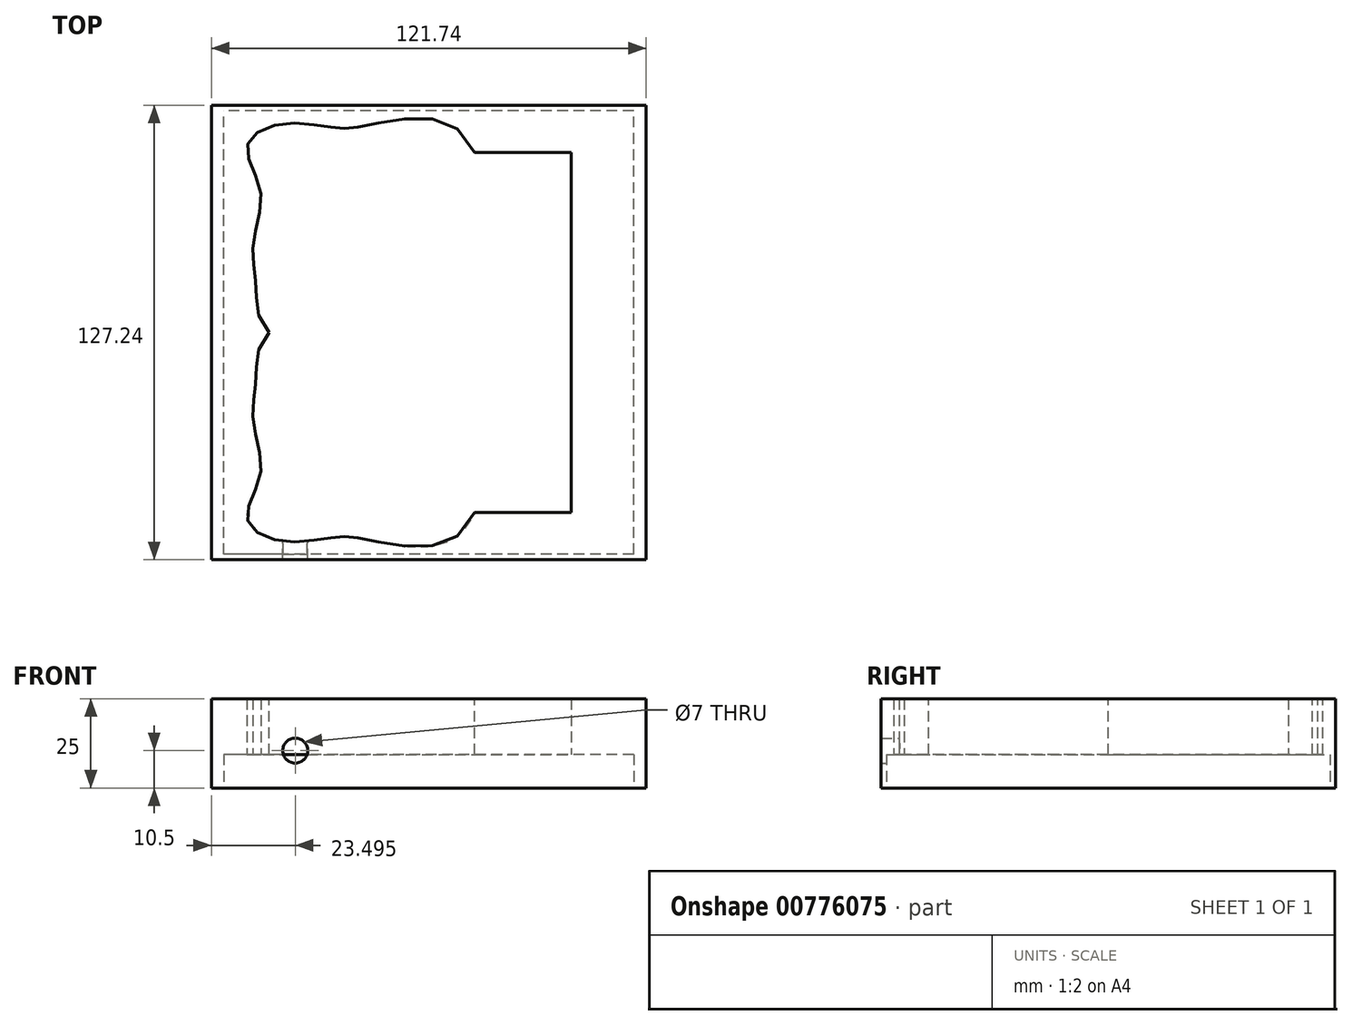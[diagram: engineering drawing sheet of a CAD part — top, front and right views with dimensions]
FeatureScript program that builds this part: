
annotation { "Feature Type Name" : "Feature", "Feature Type Description" : "" }
export const myFeature = defineFeature(function(context is Context, id is Id, definition is map)
    precondition{}
    {
        {
            var Q0;
            Q0=qCreatedBy(makeId("Top.planeOp"),FACE);
            var sketch = newSketch(context, id + "F0", { "sketchPlane" : qUnion([Q0])});
            skLineSegment(sketch, "E0.bottom", {"start": v(60.87, 63.62) * mm, "end": v(-60.87, 63.62) * mm});
            skLineSegment(sketch, "E0.top", {"start": v(60.87, -63.62) * mm, "end": v(-60.87, -63.62) * mm});
            skLineSegment(sketch, "E0.left", {"start": v(60.87, 63.62) * mm, "end": v(60.87, -63.62) * mm});
            skLineSegment(sketch, "E0.right", {"start": v(-60.87, 63.62) * mm, "end": v(-60.87, -63.62) * mm});
            skPoint(sketch, "E0.middle", {"position": v(0, 0) * mm});
            skLineSegment(sketch, "E1.bottom", {"start": v(39.88, 50.37) * mm, "end": v(-39.88, 50.37) * mm});
            skLineSegment(sketch, "E1.top", {"start": v(39.88, -50.37) * mm, "end": v(-39.88, -50.37) * mm});
            skLineSegment(sketch, "E1.left", {"start": v(39.88, 50.37) * mm, "end": v(39.88, -50.37) * mm});
            skLineSegment(sketch, "E1.right", {"start": v(-39.88, 50.37) * mm, "end": v(-39.88, -50.37) * mm});
            skSolve(sketch);
        }
        {
            var Q0;
            Q0=makeQuery(id+"F0.imprint","IMPRINT",FACE,{"disambiguationData":[TD([[makeQuery(id+"F0.imprint","IMPRINT",EDGE,{"derivedFrom":sQuery(id+"F0.wireOp",EDGE,"E0.bottom")}),1.0]])]});
            extrude(context, id + "F1", {"entities" : qUnion([Q0]), "depth" : 25 * mm, "offsetDistance" : 25 * mm});
        }
        {
            var Q0;
            Q0=qCreatedBy(makeId("Top.planeOp"),FACE);
            cPlane(context, id + "F2", {"entities" : qUnion([Q0]), "cplaneType" : CPlaneType.OFFSET, "offset" : 25 * mm, "width" : 150 * mm, "height" : 150 * mm});
        }
        {
            var Q0;
            Q0=qCreatedBy(id+"F2.planeOp",FACE);
            var sketch = newSketch(context, id + "F3", { "sketchPlane" : qUnion([Q0])});
            skFitSpline(sketch, "E2", {"points": [v(-44.75, 0) * mm, v(-48.38, 13.37) * mm, v(-49.13, 24.87) * mm, v(-47.13, 39.62) * mm, v(-50.88, 52.12) * mm, v(-41.38, 58.37) * mm, v(-26.63, 57.37) * mm, v(-17.88, 57.87) * mm, v(9.64, 55.54) * mm, v(0, -2.7) * mm, v(-44.75, 0) * mm]});
            skSolve(sketch);
        }
        {
            var Q0;
            Q0=makeQuery(id+"F3.imprint","IMPRINT",FACE,{"disambiguationData":[TD([[makeQuery(id+"F3.imprint","IMPRINT",EDGE,{"derivedFrom":sQuery(id+"F3.wireOp",EDGE,"E2")}),-1.0]])]});
            extrude(context, id + "F4", {"entities" : qUnion([Q0]), "operationType" : NewBodyOperationType.REMOVE, "oppositeDirection" : true, "depth" : 50.3 * mm, "offsetDistance" : 25 * mm});
        }
        {
            var Q0;
            Q0=qCreatedBy(makeId("Top.planeOp"),FACE);
            var sketch = newSketch(context, id + "F5", { "sketchPlane" : qUnion([Q0])});
            skLineSegment(sketch, "E3.bottom", {"start": v(85.63, 0) * mm, "end": v(-85.63, 0) * mm});
            skLineSegment(sketch, "E3.top", {"start": v(85.63, -102.26) * mm, "end": v(-85.63, -102.26) * mm});
            skLineSegment(sketch, "E3.left", {"start": v(85.63, 0) * mm, "end": v(85.63, -102.26) * mm});
            skLineSegment(sketch, "E3.right", {"start": v(-85.63, 0) * mm, "end": v(-85.63, -102.26) * mm});
            skPoint(sketch, "E3.middle", {"position": v(0, -51.13) * mm});
            skSolve(sketch);
        }
        {
            var Q0;
            Q0=makeQuery(id+"F5.imprint","IMPRINT",FACE,{"disambiguationData":[TD([[makeQuery(id+"F5.imprint","IMPRINT",EDGE,{"derivedFrom":sQuery(id+"F5.wireOp",EDGE,"E3.bottom")}),1.0]])]});
            extrude(context, id + "F6", {"entities" : qUnion([Q0]), "operationType" : NewBodyOperationType.REMOVE, "oppositeDirection" : true, "depth" : 25 * mm, "offsetDistance" : 25 * mm, "hasSecondDirection" : true, "secondDirectionOppositeDirection" : false, "secondDirectionDepth" : 25 * mm});
        }
        {
            var Q0;
            Q0=makeQuery(id+"F1.opExtrude","SWEPT_BODY",BODY,{"disambiguationData":[OSD([sQuery(id+"F0.wireOp",EDGE,"E0.bottom"),sQuery(id+"F0.wireOp",EDGE,"E0.top"),sQuery(id+"F0.wireOp",EDGE,"E0.left"),sQuery(id+"F0.wireOp",EDGE,"E0.right"),sQuery(id+"F0.wireOp",EDGE,"E1.bottom"),sQuery(id+"F0.wireOp",EDGE,"E1.top"),sQuery(id+"F0.wireOp",EDGE,"E1.left"),sQuery(id+"F0.wireOp",EDGE,"E1.right")])]});
            var Q1;
            Q1=qCreatedBy(makeId("Front.planeOp"),FACE);
            mirror(context, id + "F7", {"operationType" : NewBodyOperationType.ADD, "entities" : qUnion([Q0]), "mirrorPlane" : qUnion([Q1])});
        }
        {
            var Q0;
            Q0=makeQuery(id+"F0.imprint","IMPRINT",FACE,{"disambiguationData":[TD([[makeQuery(id+"F0.imprint","IMPRINT",EDGE,{"derivedFrom":sQuery(id+"F0.wireOp",EDGE,"E0.bottom")}),1.0]])]});
            var sketch = newSketch(context, id + "F8", { "sketchPlane" : qUnion([Q0])});
            skLineSegment(sketch, "E4.bottom", {"start": v(57.37, -62.12) * mm, "end": v(-57.37, -62.12) * mm});
            skLineSegment(sketch, "E4.top", {"start": v(57.37, 62.12) * mm, "end": v(-57.37, 62.12) * mm});
            skLineSegment(sketch, "E4.left", {"start": v(57.37, -62.12) * mm, "end": v(57.37, 62.12) * mm});
            skLineSegment(sketch, "E4.right", {"start": v(-57.37, -62.12) * mm, "end": v(-57.37, 62.12) * mm});
            skPoint(sketch, "E4.middle", {"position": v(0, 0) * mm});
            skSolve(sketch);
        }
        {
            var Q0;
            Q0 = qSketchRegion(id + "F8", true);
            extrude(context, id + "F9", {"entities" : qUnion([Q0]), "operationType" : NewBodyOperationType.REMOVE, "depth" : 9.4 * mm, "offsetDistance" : 25 * mm});
        }
        {
            var Q0;
            Q0=qCreatedBy(makeId("Front.planeOp"),FACE);
            var sketch = newSketch(context, id + "F10", { "sketchPlane" : qUnion([Q0])});
            skCircle(sketch, "E5", {"center": v(-37.37, 10.5) * mm, "radius": 3.5 * mm});
            skSolve(sketch);
        }
        {
            var Q0;
            Q0=makeQuery(id+"F10.imprint","IMPRINT",FACE,{"disambiguationData":[TD([[makeQuery(id+"F10.imprint","IMPRINT",EDGE,{"derivedFrom":sQuery(id+"F10.wireOp",EDGE,"E5")}),1.0]])]});
            var Q1;
            Q1=sQuery(id+"F10.wireOp",EDGE,"E5");
            extrude(context, id + "F11", {"entities" : qUnion([Q0]), "operationType" : NewBodyOperationType.REMOVE, "surfaceEntities" : qUnion([Q1]), "depth" : 130.8 * mm, "offsetDistance" : 25 * mm});
        }
    });
